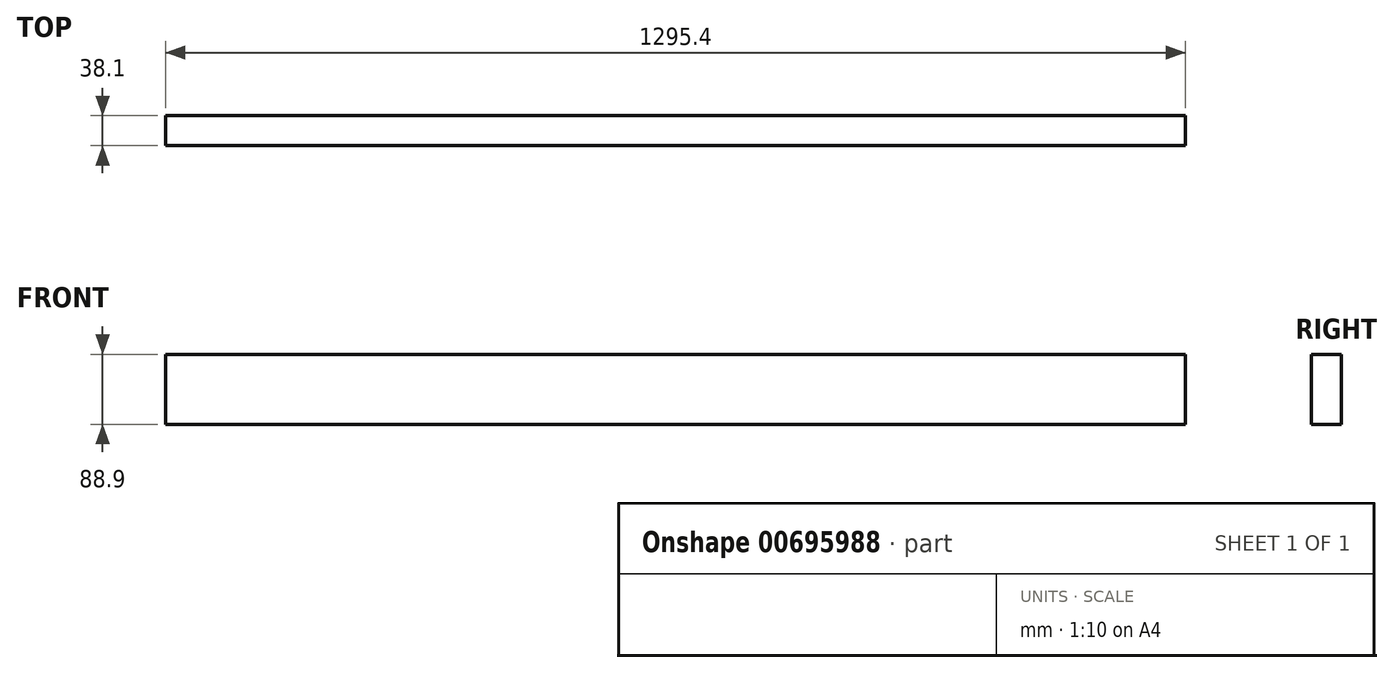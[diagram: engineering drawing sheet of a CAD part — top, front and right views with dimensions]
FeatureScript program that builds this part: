
annotation { "Feature Type Name" : "Feature", "Feature Type Description" : "" }
export const myFeature = defineFeature(function(context is Context, id is Id, definition is map)
    precondition{}
    {
        {
            var Q0;
            Q0=qCreatedBy(makeId("Front.planeOp"),FACE);
            var sketch = newSketch(context, id + "F0", { "sketchPlane" : qUnion([Q0])});
            skLineSegment(sketch, "E0.bottom", {"start": v(0, 0) * mm, "end": v(1295.4, 0) * mm});
            skLineSegment(sketch, "E0.top", {"start": v(0, 88.9) * mm, "end": v(1295.4, 88.9) * mm});
            skLineSegment(sketch, "E0.left", {"start": v(0, 0) * mm, "end": v(0, 88.9) * mm});
            skLineSegment(sketch, "E0.right", {"start": v(1295.4, 0) * mm, "end": v(1295.4, 88.9) * mm});
            skSolve(sketch);
        }
        {
            var Q0;
            Q0=makeQuery(id+"F0.imprint","IMPRINT",FACE,{"disambiguationData":[TD([[makeQuery(id+"F0.imprint","IMPRINT",EDGE,{"derivedFrom":sQuery(id+"F0.wireOp",EDGE,"E0.bottom")}),1.0]])]});
            extrude(context, id + "F1", {"entities" : qUnion([Q0]), "depth" : 38.1 * mm, "offsetDistance" : 25.4 * mm});
        }
    });
